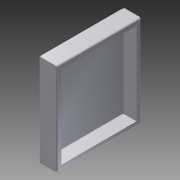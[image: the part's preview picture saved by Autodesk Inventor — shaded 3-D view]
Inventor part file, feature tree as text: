
AUTODESK INVENTOR PART (.ipt)
format: ipt  version: 2015 (Build 190159000, 159)  size: 344,064 bytes
history: native  units: mm
features: sheet_metal_op x11, other x5, sketch x3
ambient origin geometry x8: Origin, YZ Plane, XZ Plane, XY Plane, X Axis, Y Axis, Z Axis, Center Point
bodies: Solid1 (feature_tree)
feature tree (19):
  sheet_metal_op  "Face1"
  sheet_metal_op  "Flange1"
  other  "A-Side Definition"
  sheet_metal_op  "Flange3"
  sketch  "Sketch1"  dims[d0=220.0mm]
  other  "Plate1"
  sketch  "Sketch2"  dims[d1=240.0mm]
  other  "Plate2"
  sheet_metal_op  "Bend1"
  sheet_metal_op  "Corner1"
  sketch  "Sketch4"  dims[d2=1.6mm d3=1.6mm d4=0.8mm d5=3.2mm d6=1.6mm d7=47.0mm d8=90.0deg d9=1.6mm d10=6.4mm d11=1.6mm d12=1.6mm d33=6.4mm d34=1.6mm d35=0.1mm d36=0.0mm d37=10.0mm d38=6.4mm d39=1.6mm d40=0.1mm d41=0.0mm d42=10.0mm d43=6.4mm d44=1.6mm d45=0.1mm d46=0.0mm d47=10.0mm d48=6.4mm d49=1.6mm d50=0.1mm d51=0.0mm d52=10.0mm d53=1.6mm d54=0.8mm d55=3.2mm d56=1.6mm d57=12.0mm d58=90.0deg d59=1.6mm d60=6.4mm d61=0.1mm d62=1.6mm]
  other  "Plate4"
  sheet_metal_op  "Bend3"
  sheet_metal_op  "Corner3"
  sheet_metal_op  "Corner5"
  sheet_metal_op  "Corner6"
  sheet_metal_op  "Corner7"
  sheet_metal_op  "Corner8"
  other  "Definition1"
